# Revit family: Lilja 12W Surface mount
name_source: partatom
category: Lighting Fixtures
revit_build: Autodesk Revit 2018 (Build: 20170525_2315(x64)
units: mm (PartAtom-declared; Revit-internal decimal feet)

## family parameters
Cut with Voids When Loaded = No
Host = Face
Light Source = Yes
OmniClass Number = 23.80.70.11.11
OmniClass Title = General Luminaries, Non Directional
Part Type = Normal
Room Calculation Point = No
Round Connector Dimension = Use Diameter
Shared = No

## types (2) — shared parameters
Beam Angle = 120°
CRI = 80
Casing Color = White
Color Filter = 16777215
Cutout = -
Default Elevation = 1219 mm
Depth = -
Description = Downlight
Dimensions = 170mm x 36mm
Dimmable = Yes
Dimming Lamp Color Temperature Shift = <None>
Directivity = No
Driver = Separate
Housing Material = Aluminium
IP Code = IP40
Lamp = LED
Last Updated = 25.2.2016
Lifetime L70 = 50000h
Manufacturer = Winled Oy Ltd
Model = Lilja 12W surface
Operating Temperature Range = -20° to +40°C
Tilt Angle = -90.00°
Type Image = Lilja 12W pinta.png
URL = www.winled.fi
Voltage = 230 V
Wattage Comments = 12W

## per-type parameters (varying)
| type | Color Temperature | Lumens Output | Photometric Web File | Product Number |
| Lilja 12W Surface mount, Neutral White, 230V - 02PP996N011R01 | 4000K | 930lm | Lilja 12W NV pinta.ies | 02PP996N011R01 |
| Lilja 12W Surface mount, Warm White, 230V - 02PP996L011R01 | 3000K | 849lm | Lilja 12W LV pinta.ies | 02PP996L011R01 |

## geometry (parser evidence)
native form markers: Sweep x5
no freeform markers — native parametric forms only
